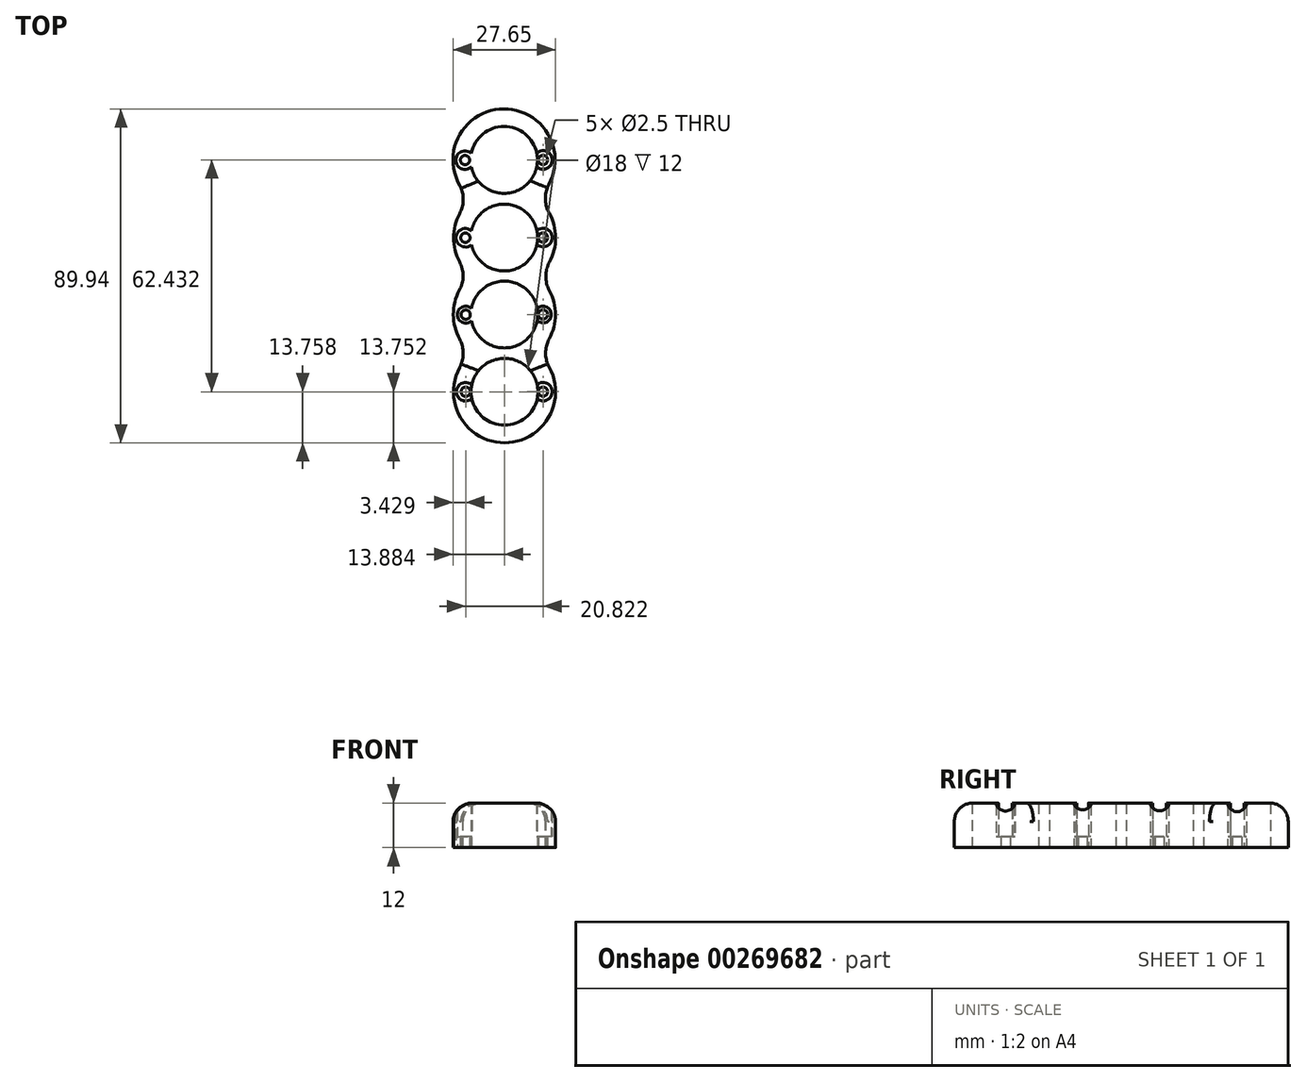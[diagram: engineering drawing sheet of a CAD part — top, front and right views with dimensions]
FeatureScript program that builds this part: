
annotation { "Feature Type Name" : "Feature", "Feature Type Description" : "" }
export const myFeature = defineFeature(function(context is Context, id is Id, definition is map)
    precondition{}
    {
        {
            var Q0;
            Q0=qCreatedBy(makeId("Top.planeOp"),FACE);
            var sketch = newSketch(context, id + "F0", { "sketchPlane" : qUnion([Q0])});
            skLineSegment(sketch, "E0", {"start": v(-16.59, 32.32) * mm, "end": v(-16.41, -49.3) * mm, "construction": true});
            skCircle(sketch, "E1", {"center": v(-16.47, -23.03) * mm, "radius": 9 * mm});
            skCircle(sketch, "E2", {"center": v(-16.51, -2.3) * mm, "radius": 9 * mm});
            skCircle(sketch, "E3", {"center": v(-16.56, 18.6) * mm, "radius": 9 * mm});
            skPoint(sketch, "E4.oppositeSnap0", {"position": v(-7.5, -35.15) * mm});
            skPoint(sketch, "E5.endSnap0", {"position": v(-29.5, -35.15) * mm});
            skCircle(sketch, "E6", {"center": v(-6.06, 18.6) * mm, "radius": 1.25 * mm});
            skCircle(sketch, "E7", {"center": v(-6.06, -2.3) * mm, "radius": 1.25 * mm});
            skCircle(sketch, "E8", {"center": v(-6.06, -23.03) * mm, "radius": 1.25 * mm});
            skCircle(sketch, "E9.MirrorC", {"center": v(-27.06, 18.56) * mm, "radius": 1.25 * mm});
            skCircle(sketch, "E10.MirrorC", {"center": v(-26.97, -2.35) * mm, "radius": 1.25 * mm});
            skCircle(sketch, "E11.MirrorC", {"center": v(-26.88, -23.07) * mm, "radius": 1.25 * mm});
            skCircle(sketch, "E12", {"center": v(-6.06, -43.8) * mm, "radius": 1.25 * mm});
            skCircle(sketch, "E13", {"center": v(-26.88, -43.83) * mm, "radius": 1.25 * mm});
            skCircle(sketch, "E14", {"center": v(-16.43, -43.84) * mm, "radius": 9 * mm});
            skLineSegment(sketch, "E15", {"start": v(-16.51, -2.3) * mm, "end": v(-39.55, -2.35) * mm, "construction": true});
            skLineSegment(sketch, "E16", {"start": v(-16.47, -23.03) * mm, "end": v(-37.2, -23.07) * mm, "construction": true});
            skLineSegment(sketch, "E17", {"start": v(-3.61, -22.63) * mm, "end": v(-3.61, -23.37) * mm});
            skLineSegment(sketch, "E18", {"start": v(-29.44, -22.8) * mm, "end": v(-29.44, -23.31) * mm});
            skLineSegment(sketch, "E19", {"start": v(-29.78, -2.22) * mm, "end": v(-29.77, -2.45) * mm});
            skLineSegment(sketch, "E20", {"start": v(-3.22, -2.2) * mm, "end": v(-3.22, -2.36) * mm});
            skCircle(sketch, "E21", {"center": v(-26.88, -23.07) * mm, "radius": 2.25 * mm});
            skCircle(sketch, "E22", {"center": v(-6.06, -23.03) * mm, "radius": 2.25 * mm});
            skPoint(sketch, "E23.startSnap0", {"position": v(-25.4, -12.84) * mm});
            skPoint(sketch, "E23.endSnap0", {"position": v(-25.36, -33.39) * mm});
            skPoint(sketch, "E24.startSnap0", {"position": v(-25.45, 8.1) * mm});
            skCircle(sketch, "E25", {"center": v(-16.56, 18.6) * mm, "radius": 13.75 * mm});
            skCircle(sketch, "E26", {"center": v(-16.43, -43.84) * mm, "radius": 13.75 * mm});
            skCircle(sketch, "E27", {"center": v(-26.97, -2.35) * mm, "radius": 2.5 * mm});
            skCircle(sketch, "E28", {"center": v(-6.06, -2.3) * mm, "radius": 2.5 * mm});
            skCircle(sketch, "E29", {"center": v(-6.06, 18.6) * mm, "radius": 2.5 * mm});
            skCircle(sketch, "E30", {"center": v(-27.06, 18.56) * mm, "radius": 2.5 * mm});
            skCircle(sketch, "E31", {"center": v(-26.88, -43.83) * mm, "radius": 2.5 * mm});
            skCircle(sketch, "E32", {"center": v(-6.06, -43.8) * mm, "radius": 2.5 * mm});
            skCircle(sketch, "E33", {"center": v(-16.47, -23.03) * mm, "radius": 13.75 * mm});
            skCircle(sketch, "E34", {"center": v(-16.41, -2.37) * mm, "radius": 13.75 * mm});
            skSolve(sketch);
        }
        {
            var Q0;
            {var subQ0=sQuery(id+"F0.wireOp",EDGE,"E26");var subQ1=sQuery(id+"F0.wireOp",EDGE,"E1");var subQ2=makeQuery(id+"F0.imprint","INTERSECT",VERTEX,{"disambiguationData":[OD(0.0)],"derivedFrom":[subQ1,subQ0]});Q0=makeQuery(id+"F0.imprint","IMPRINT",FACE,{"disambiguationData":[TD([[makeQuery(id+"F0.imprint","IMPRINT",EDGE,{"disambiguationData":[TD([[subQ2,-1.0]])],"derivedFrom":subQ1}),-1.0]])]});}
            var Q1;
            {var subQ0=sQuery(id+"F0.wireOp",EDGE,"E25");var subQ1=sQuery(id+"F0.wireOp",EDGE,"E2");var subQ2=makeQuery(id+"F0.imprint","INTERSECT",VERTEX,{"disambiguationData":[OD(0.0)],"derivedFrom":[subQ1,subQ0]});Q1=makeQuery(id+"F0.imprint","IMPRINT",FACE,{"disambiguationData":[TD([[makeQuery(id+"F0.imprint","IMPRINT",EDGE,{"disambiguationData":[TD([[subQ2,-1.0]])],"derivedFrom":subQ1}),-1.0]])]});}
            var Q2;
            {var subQ0=sQuery(id+"F0.wireOp",EDGE,"E34");var subQ7=sQuery(id+"F0.wireOp",EDGE,"E1");var subQ8=makeQuery(id+"F0.imprint","INTERSECT",VERTEX,{"disambiguationData":[OD(0.0)],"derivedFrom":[subQ7,subQ0]});Q2=makeQuery(id+"F0.imprint","IMPRINT",FACE,{"disambiguationData":[TD([[makeQuery(id+"F0.imprint","IMPRINT",EDGE,{"disambiguationData":[TD([[subQ8,-1.0]])],"derivedFrom":subQ7}),-1.0]])]});}
            var Q3;
            {var subQ1=sQuery(id+"F0.wireOp",EDGE,"E2");var subQ5=sQuery(id+"F0.wireOp",EDGE,"E25");var subQ7=makeQuery(id+"F0.imprint","INTERSECT",VERTEX,{"disambiguationData":[OD(0.0)],"derivedFrom":[subQ1,subQ5]});Q3=makeQuery(id+"F0.imprint","IMPRINT",FACE,{"disambiguationData":[TD([[makeQuery(id+"F0.imprint","IMPRINT",EDGE,{"disambiguationData":[TD([[subQ7,1.0]])],"derivedFrom":subQ1}),-1.0]])]});}
            var Q4;
            {var subQ1=sQuery(id+"F0.wireOp",EDGE,"E2");var subQ7=sQuery(id+"F0.wireOp",EDGE,"E25");var subQ9=makeQuery(id+"F0.imprint","INTERSECT",VERTEX,{"disambiguationData":[OD(1.0)],"derivedFrom":[subQ1,subQ7]});Q4=makeQuery(id+"F0.imprint","IMPRINT",FACE,{"disambiguationData":[TD([[makeQuery(id+"F0.imprint","IMPRINT",EDGE,{"disambiguationData":[TD([[subQ9,-1.0]])],"derivedFrom":subQ1}),-1.0]])]});}
            var Q5;
            {var subQ3=sQuery(id+"F0.wireOp",EDGE,"E1");var subQ5=sQuery(id+"F0.wireOp",EDGE,"E34");var subQ6=makeQuery(id+"F0.imprint","INTERSECT",VERTEX,{"disambiguationData":[OD(1.0)],"derivedFrom":[subQ3,subQ5]});Q5=makeQuery(id+"F0.imprint","IMPRINT",FACE,{"disambiguationData":[TD([[makeQuery(id+"F0.imprint","IMPRINT",EDGE,{"disambiguationData":[TD([[subQ6,-1.0]])],"derivedFrom":subQ3}),-1.0]])]});}
            var Q6;
            {var subQ3=sQuery(id+"F0.wireOp",EDGE,"E1");var subQ5=sQuery(id+"F0.wireOp",EDGE,"E34");var subQ6=makeQuery(id+"F0.imprint","INTERSECT",VERTEX,{"disambiguationData":[OD(0.0)],"derivedFrom":[subQ3,subQ5]});Q6=makeQuery(id+"F0.imprint","IMPRINT",FACE,{"disambiguationData":[TD([[makeQuery(id+"F0.imprint","IMPRINT",EDGE,{"disambiguationData":[TD([[subQ6,1.0]])],"derivedFrom":subQ3}),-1.0]])]});}
            var Q7;
            {var subQ1=sQuery(id+"F0.wireOp",EDGE,"E14");var subQ6=sQuery(id+"F0.wireOp",EDGE,"E33");var subQ11=makeQuery(id+"F0.imprint","INTERSECT",VERTEX,{"disambiguationData":[OD(0.0)],"derivedFrom":[subQ1,subQ6]});Q7=makeQuery(id+"F0.imprint","IMPRINT",FACE,{"disambiguationData":[TD([[makeQuery(id+"F0.imprint","IMPRINT",EDGE,{"disambiguationData":[TD([[subQ11,1.0]])],"derivedFrom":subQ1}),-1.0]])]});}
            var Q8;
            {var subQ1=sQuery(id+"F0.wireOp",EDGE,"E3");var subQ9=sQuery(id+"F0.wireOp",EDGE,"E30");var subQ10=makeQuery(id+"F0.imprint","INTERSECT",VERTEX,{"disambiguationData":[OD(0.0)],"derivedFrom":[subQ1,subQ9]});Q8=makeQuery(id+"F0.imprint","IMPRINT",FACE,{"disambiguationData":[TD([[makeQuery(id+"F0.imprint","IMPRINT",EDGE,{"disambiguationData":[TD([[subQ10,1.0]])],"derivedFrom":subQ1}),-1.0]])]});}
            extrude(context, id + "F1", {"entities" : qUnion([Q0, Q1, Q2, Q3, Q4, Q5, Q6, Q7, Q8]), "depth" : 12 * mm});
        }
        {
            var Q0;
            Q0=makeQuery(id+"F0.imprint","IMPRINT",FACE,{"disambiguationData":[TD([[makeQuery(id+"F0.imprint","IMPRINT",EDGE,{"derivedFrom":sQuery(id+"F0.wireOp",EDGE,"E8")}),-1.0]])]});
            var Q1;
            {var subQ0=sQuery(id+"F0.wireOp",EDGE,"E21");var subQ1=sQuery(id+"F0.wireOp",EDGE,"073f5de2-028e-462f-9cef-9b1b6fd825d90.MirrorCS");var subQ2=makeQuery(id+"F0.imprint","INTERSECT",VERTEX,{"disambiguationData":[OD(0.0)],"derivedFrom":[subQ1,subQ0]});Q1=makeQuery(id+"F0.imprint","IMPRINT",FACE,{"disambiguationData":[TD([[makeQuery(id+"F0.imprint","IMPRINT",EDGE,{"disambiguationData":[TD([[subQ2,-1.0]])],"derivedFrom":subQ1}),-1.0]])]});}
            var Q2;
            Q2=makeQuery(id+"F0.imprint","IMPRINT",FACE,{"disambiguationData":[TD([[makeQuery(id+"F0.imprint","IMPRINT",EDGE,{"derivedFrom":sQuery(id+"F0.wireOp",EDGE,"E11.MirrorC")}),1.0]])]});
            var Q3;
            {var subQ0=sQuery(id+"F0.wireOp",EDGE,"E21");var subQ1=sQuery(id+"F0.wireOp",EDGE,"d793a48b-257a-4737-bc45-a45dbda491930.MirrorCS");var subQ2=makeQuery(id+"F0.imprint","INTERSECT",VERTEX,{"disambiguationData":[OD(0.0)],"derivedFrom":[subQ1,subQ0]});Q3=makeQuery(id+"F0.imprint","IMPRINT",FACE,{"disambiguationData":[TD([[makeQuery(id+"F0.imprint","IMPRINT",EDGE,{"disambiguationData":[TD([[subQ2,-1.0]])],"derivedFrom":subQ1}),1.0]])]});}
            var Q4;
            {var subQ0=sQuery(id+"F0.wireOp",EDGE,"E22");var subQ1=sQuery(id+"F0.wireOp",EDGE,"3404ae05-0c8b-4081-b07d-0651607c9c130.MirrorCS");var subQ2=makeQuery(id+"F0.imprint","INTERSECT",VERTEX,{"disambiguationData":[OD(0.0)],"derivedFrom":[subQ1,subQ0]});Q4=makeQuery(id+"F0.imprint","IMPRINT",FACE,{"disambiguationData":[TD([[makeQuery(id+"F0.imprint","IMPRINT",EDGE,{"disambiguationData":[TD([[subQ2,-1.0]])],"derivedFrom":subQ1}),-1.0]])]});}
            var Q5;
            {var subQ0=sQuery(id+"F0.wireOp",EDGE,"E22");var subQ1=sQuery(id+"F0.wireOp",EDGE,"kTRhAb7x-PPG7-BJcY-bXVo-2Zxu0mkdpO8j");var subQ2=makeQuery(id+"F0.imprint","INTERSECT",VERTEX,{"disambiguationData":[OD(0.0)],"derivedFrom":[subQ1,subQ0]});Q5=makeQuery(id+"F0.imprint","IMPRINT",FACE,{"disambiguationData":[TD([[makeQuery(id+"F0.imprint","IMPRINT",EDGE,{"disambiguationData":[TD([[subQ2,-1.0]])],"derivedFrom":subQ1}),1.0]])]});}
            var Q6;
            Q6=makeQuery(id+"F0.imprint","IMPRINT",FACE,{"disambiguationData":[TD([[makeQuery(id+"F0.imprint","IMPRINT",EDGE,{"derivedFrom":sQuery(id+"F0.wireOp",EDGE,"E10.MirrorC")}),1.0]])]});
            var Q7;
            Q7=makeQuery(id+"F0.imprint","IMPRINT",FACE,{"disambiguationData":[TD([[makeQuery(id+"F0.imprint","IMPRINT",EDGE,{"derivedFrom":sQuery(id+"F0.wireOp",EDGE,"E7")}),-1.0]])]});
            var Q8;
            Q8=makeQuery(id+"F0.imprint","IMPRINT",FACE,{"disambiguationData":[TD([[makeQuery(id+"F0.imprint","IMPRINT",EDGE,{"derivedFrom":sQuery(id+"F0.wireOp",EDGE,"E6")}),-1.0]])]});
            var Q9;
            Q9=makeQuery(id+"F0.imprint","IMPRINT",FACE,{"disambiguationData":[TD([[makeQuery(id+"F0.imprint","IMPRINT",EDGE,{"derivedFrom":sQuery(id+"F0.wireOp",EDGE,"E9.MirrorC")}),1.0]])]});
            var Q10;
            Q10=makeQuery(id+"F0.imprint","IMPRINT",FACE,{"disambiguationData":[TD([[makeQuery(id+"F0.imprint","IMPRINT",EDGE,{"derivedFrom":sQuery(id+"F0.wireOp",EDGE,"E13")}),-1.0]])]});
            var Q11;
            Q11=makeQuery(id+"F0.imprint","IMPRINT",FACE,{"disambiguationData":[TD([[makeQuery(id+"F0.imprint","IMPRINT",EDGE,{"derivedFrom":sQuery(id+"F0.wireOp",EDGE,"E12")}),-1.0]])]});
            extrude(context, id + "F2", {"entities" : qUnion([Q0, Q1, Q2, Q3, Q4, Q5, Q6, Q7, Q8, Q9, Q10, Q11]), "operationType" : NewBodyOperationType.ADD, "depth" : 3 * mm});
        }
        {
            var Q0;
            {var subQ0=sQuery(id+"F0.wireOp",EDGE,"E33");var subQ1=sQuery(id+"F0.wireOp",EDGE,"E26");Q0=makeQuery(id+"F1.opExtrude","SWEPT_EDGE",EDGE,{"disambiguationData":[OSD([subQ1,subQ0]),TDD([makeQuery(id+"F0.imprint","INTERSECT",VERTEX,{"disambiguationData":[OD(0.0)],"derivedFrom":[subQ1,subQ0]})])]});}
            var Q1;
            {var subQ0=sQuery(id+"F0.wireOp",EDGE,"E34");var subQ1=sQuery(id+"F0.wireOp",EDGE,"E33");Q1=makeQuery(id+"F1.opExtrude","SWEPT_EDGE",EDGE,{"disambiguationData":[OSD([subQ1,subQ0]),TDD([makeQuery(id+"F0.imprint","INTERSECT",VERTEX,{"disambiguationData":[OD(0.0)],"derivedFrom":[subQ1,subQ0]})])]});}
            var Q2;
            {var subQ0=sQuery(id+"F0.wireOp",EDGE,"E34");var subQ1=sQuery(id+"F0.wireOp",EDGE,"E25");Q2=makeQuery(id+"F1.opExtrude","SWEPT_EDGE",EDGE,{"disambiguationData":[OSD([subQ1,subQ0]),TDD([makeQuery(id+"F0.imprint","INTERSECT",VERTEX,{"disambiguationData":[OD(1.0)],"derivedFrom":[subQ1,subQ0]})])]});}
            var Q3;
            {var subQ0=sQuery(id+"F0.wireOp",EDGE,"E34");var subQ1=sQuery(id+"F0.wireOp",EDGE,"E25");Q3=makeQuery(id+"F1.opExtrude","SWEPT_EDGE",EDGE,{"disambiguationData":[OSD([subQ1,subQ0]),TDD([makeQuery(id+"F0.imprint","INTERSECT",VERTEX,{"disambiguationData":[OD(0.0)],"derivedFrom":[subQ1,subQ0]})])]});}
            var Q4;
            {var subQ0=sQuery(id+"F0.wireOp",EDGE,"E34");var subQ1=sQuery(id+"F0.wireOp",EDGE,"E33");Q4=makeQuery(id+"F1.opExtrude","SWEPT_EDGE",EDGE,{"disambiguationData":[OSD([subQ1,subQ0]),TDD([makeQuery(id+"F0.imprint","INTERSECT",VERTEX,{"disambiguationData":[OD(1.0)],"derivedFrom":[subQ1,subQ0]})])]});}
            var Q5;
            {var subQ0=sQuery(id+"F0.wireOp",EDGE,"E33");var subQ1=sQuery(id+"F0.wireOp",EDGE,"E26");Q5=makeQuery(id+"F1.opExtrude","SWEPT_EDGE",EDGE,{"disambiguationData":[OSD([subQ1,subQ0]),TDD([makeQuery(id+"F0.imprint","INTERSECT",VERTEX,{"disambiguationData":[OD(1.0)],"derivedFrom":[subQ1,subQ0]})])]});}
            fillet(context, id + "F3", {"entities" : qUnion([Q0, Q1, Q2, Q3, Q4, Q5]), "radius" : 8 * mm, "tangentPropagation" : true, "allowEdgeOverflow" : false});
        }
        {
            var Q0;
            Q0=makeQuery(id+"F1.opExtrude","CAP_EDGE",EDGE,{"disambiguationData":[OSD([sQuery(id+"F0.wireOp",EDGE,"E26")])],"isStart":false});
            fillet(context, id + "F4", {"entities" : qUnion([Q0]), "radius" : 5 * mm, "tangentPropagation" : true, "allowEdgeOverflow" : false});
        }
    });
